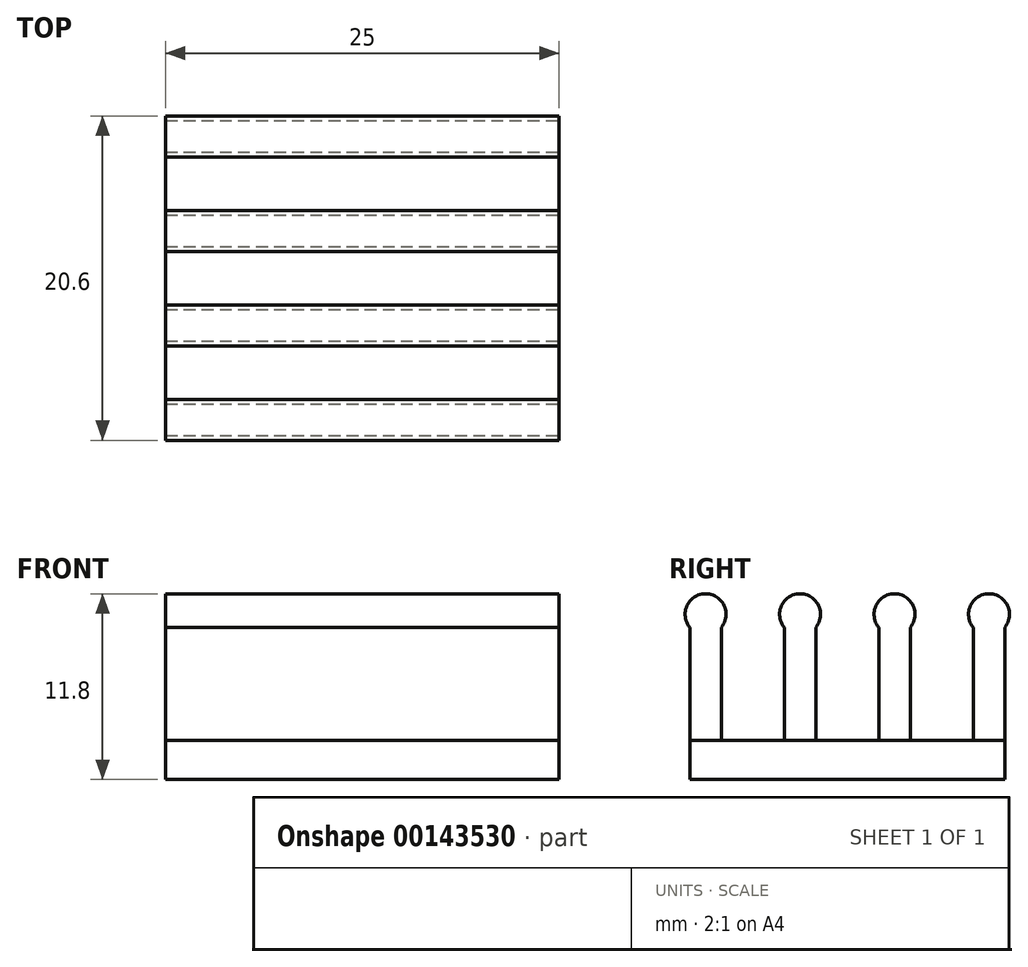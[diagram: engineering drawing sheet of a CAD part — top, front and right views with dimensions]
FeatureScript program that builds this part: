
annotation { "Feature Type Name" : "Feature", "Feature Type Description" : "" }
export const myFeature = defineFeature(function(context is Context, id is Id, definition is map)
    precondition{}
    {
        {
            var Q0;
            Q0=qCreatedBy(makeId("Top.planeOp"),FACE);
            var sketch = newSketch(context, id + "F0", { "sketchPlane" : qUnion([Q0])});
            skLineSegment(sketch, "E0.bottom", {"start": v(-12.5, 10) * mm, "end": v(12.5, 10) * mm});
            skLineSegment(sketch, "E0.top", {"start": v(-12.5, -10) * mm, "end": v(12.5, -10) * mm});
            skLineSegment(sketch, "E0.left", {"start": v(-12.5, 10) * mm, "end": v(-12.5, -10) * mm});
            skLineSegment(sketch, "E0.right", {"start": v(12.5, 10) * mm, "end": v(12.5, -10) * mm});
            skSolve(sketch);
        }
        {
            var Q0;
            Q0 = qSketchRegion(id + "F0", true);
            extrude(context, id + "F1", {"entities" : qUnion([Q0]), "depth" : 2.5 * mm});
        }
        {
            var Q0;
            Q0=makeQuery(id+"F1.opExtrude","SWEPT_FACE",FACE,{"disambiguationData":[OSD([sQuery(id+"F0.wireOp",EDGE,"E0.right")])]});
            var sketch = newSketch(context, id + "F2", { "sketchPlane" : qUnion([Q0])});
            skLineSegment(sketch, "E1.bottom", {"start": v(-10, 2.5) * mm, "end": v(-8, 2.5) * mm});
            skLineSegment(sketch, "E1.top", {"start": v(-10, 10.5) * mm, "end": v(-8, 10.5) * mm});
            skLineSegment(sketch, "E1.left", {"start": v(-10, 2.5) * mm, "end": v(-10, 10.5) * mm});
            skLineSegment(sketch, "E1.right", {"start": v(-8, 2.5) * mm, "end": v(-8, 10.5) * mm});
            skLineSegment(sketch, "E2.bottom", {"start": v(10, 2.5) * mm, "end": v(8, 2.5) * mm});
            skLineSegment(sketch, "E2.top", {"start": v(10, 10.5) * mm, "end": v(8, 10.5) * mm});
            skLineSegment(sketch, "E2.left", {"start": v(10, 2.5) * mm, "end": v(10, 10.5) * mm});
            skLineSegment(sketch, "E2.right", {"start": v(8, 2.5) * mm, "end": v(8, 10.5) * mm});
            skLineSegment(sketch, "E3.bottom", {"start": v(-4, 2.5) * mm, "end": v(-2, 2.5) * mm});
            skLineSegment(sketch, "E3.top", {"start": v(-4, 10.5) * mm, "end": v(-2, 10.5) * mm});
            skLineSegment(sketch, "E3.left", {"start": v(-4, 2.5) * mm, "end": v(-4, 10.5) * mm});
            skLineSegment(sketch, "E3.right", {"start": v(-2, 2.5) * mm, "end": v(-2, 10.5) * mm});
            skLineSegment(sketch, "E4.bottom", {"start": v(2, 2.5) * mm, "end": v(4, 2.5) * mm});
            skLineSegment(sketch, "E4.top", {"start": v(2, 10.5) * mm, "end": v(4, 10.5) * mm});
            skLineSegment(sketch, "E4.left", {"start": v(2, 2.5) * mm, "end": v(2, 10.5) * mm});
            skLineSegment(sketch, "E4.right", {"start": v(4, 2.5) * mm, "end": v(4, 10.5) * mm});
            skCircle(sketch, "E5", {"center": v(-9, 10.5) * mm, "radius": 1.3 * mm});
            skCircle(sketch, "E6", {"center": v(-3, 10.5) * mm, "radius": 1.3 * mm});
            skCircle(sketch, "E7", {"center": v(3, 10.5) * mm, "radius": 1.3 * mm});
            skCircle(sketch, "E8", {"center": v(9, 10.5) * mm, "radius": 1.3 * mm});
            skSolve(sketch);
        }
        {
            var Q0;
            Q0 = qSketchRegion(id + "F2", true);
            extrude(context, id + "F3", {"entities" : qUnion([Q0]), "oppositeDirection" : true, "depth" : 25 * mm});
        }
    });
